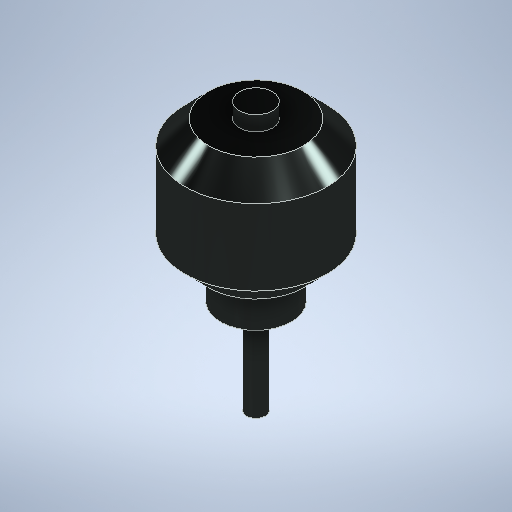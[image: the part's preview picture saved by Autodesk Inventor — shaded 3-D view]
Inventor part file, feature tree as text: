
AUTODESK INVENTOR PART (.ipt)
format: ipt  version: 2025.1 (Build 291241020, 241B)  size: 260,096 bytes
history: native  units: in
note: dims shown in document units (in); Inventor stores cm internally (conversion verified against a paired STEP export)
features: extrude x4, sketch x4, chamfer x2
ambient origin geometry x8: Origin, YZ Plane, XZ Plane, XY Plane, X Axis, Y Axis, Z Axis, Center Point
bodies: Solid1 (feature_tree)
feature tree (10):
  extrude  "Extrusion1"  Depth=2.0472in TaperAngle=0.0deg
  extrude  "Extrusion2"  Depth=0.248in TaperAngle=0.0deg
  extrude  "Extrusion3"  Depth=0.5906in TaperAngle=0.0deg
  extrude  "Extrusion4"  Depth=1.5748in TaperAngle=0.0deg
  chamfer  "Chamfer1"  Distance=0.3937in Angle=45.0deg
  chamfer  "Chamfer2"  Distance=0.3937in Angle=45.0deg
  sketch  "Sketch1"  dims[d0=2.3622in d1=2.0472in d2=0.0in]
  sketch  "Sketch2"  dims[d3=0.5512in d4=0.248in d5=0.0in]
  sketch  "Sketch3"  dims[d6=1.1811in d7=0.5906in d8=0.0in]
  sketch  "Sketch4"  dims[d9=0.315in d10=1.5748in d11=0.0in d12=0.3937in d13=0.125in d14=45.0deg d15=0.3937in d16=0.125in d17=45.0deg]
